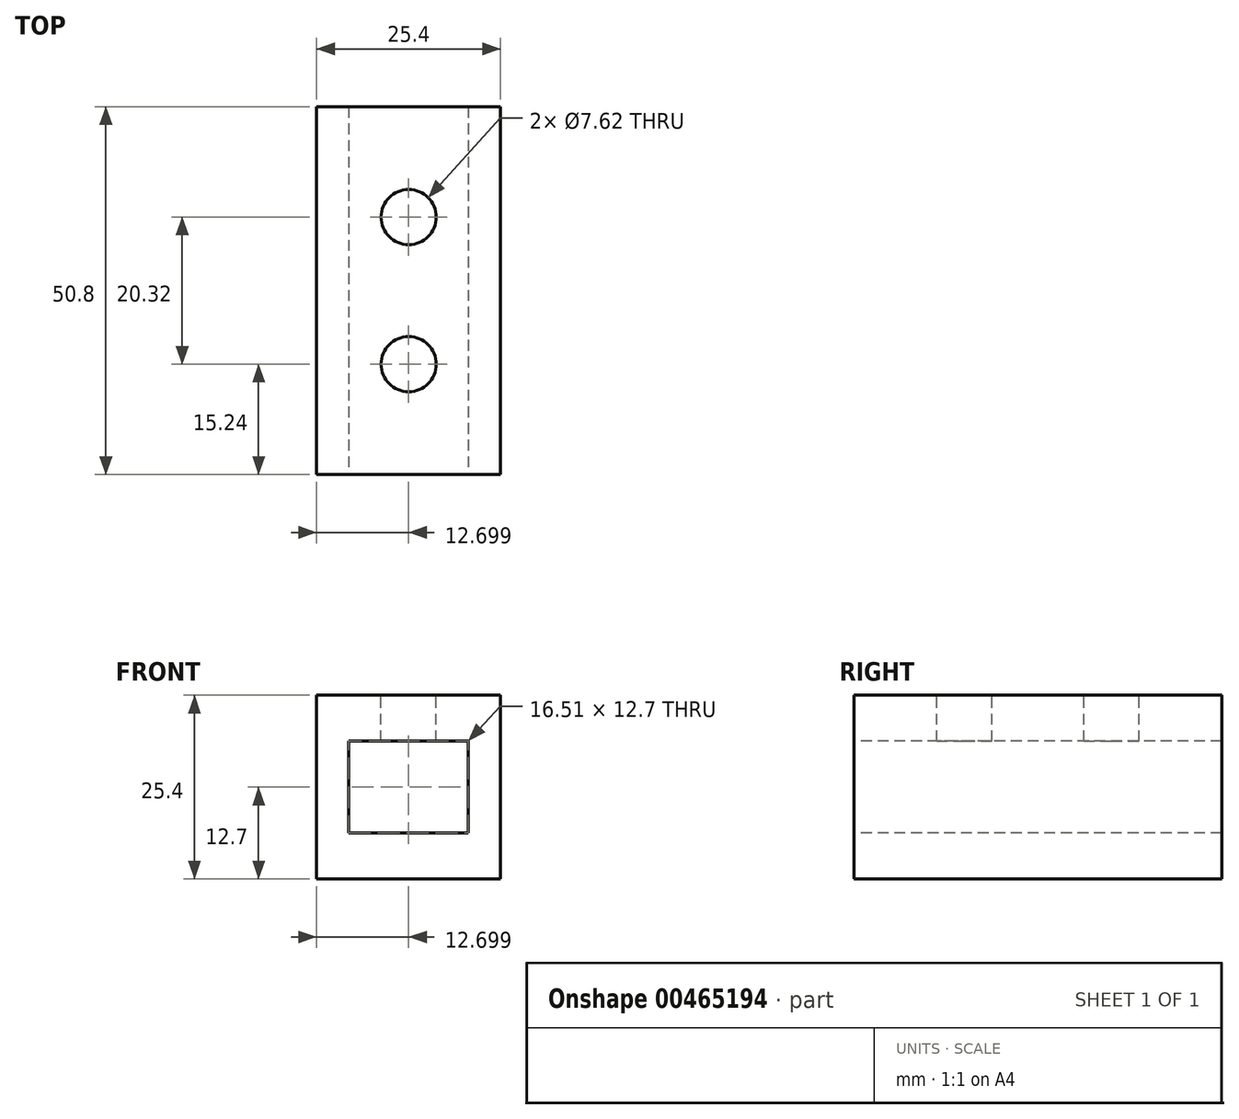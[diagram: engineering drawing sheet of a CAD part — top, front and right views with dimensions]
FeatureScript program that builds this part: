
annotation { "Feature Type Name" : "Feature", "Feature Type Description" : "" }
export const myFeature = defineFeature(function(context is Context, id is Id, definition is map)
    precondition{}
    {
        {
            var Q0;
            Q0=qCreatedBy(makeId("Top.planeOp"),FACE);
            var sketch = newSketch(context, id + "F0", { "sketchPlane" : qUnion([Q0])});
            skLineSegment(sketch, "E0.bottom", {"start": v(14.94, 25.4) * mm, "end": v(-10.46, 25.4) * mm});
            skLineSegment(sketch, "E0.top", {"start": v(14.94, -25.4) * mm, "end": v(-10.46, -25.4) * mm});
            skLineSegment(sketch, "E0.left", {"start": v(14.94, 25.4) * mm, "end": v(14.94, -25.4) * mm});
            skLineSegment(sketch, "E0.right", {"start": v(-10.46, 25.4) * mm, "end": v(-10.46, -25.4) * mm});
            skPoint(sketch, "E0.middle", {"position": v(2.24, 0) * mm});
            skSolve(sketch);
        }
        {
            var Q0;
            Q0=makeQuery(id+"F0.imprint","IMPRINT",FACE,{"disambiguationData":[TD([[makeQuery(id+"F0.imprint","IMPRINT",EDGE,{"derivedFrom":sQuery(id+"F0.wireOp",EDGE,"E0.bottom")}),1.0]])]});
            extrude(context, id + "F1", {"entities" : qUnion([Q0]), "depth" : 25.4 * mm});
        }
        {
            var Q0;
            Q0=makeQuery(id+"F1.opExtrude","SWEPT_FACE",FACE,{"disambiguationData":[OSD([sQuery(id+"F0.wireOp",EDGE,"E0.top")])]});
            var sketch = newSketch(context, id + "F2", { "sketchPlane" : qUnion([Q0])});
            skLineSegment(sketch, "E1.bottom", {"start": v(10.5, 19.05) * mm, "end": v(-6.02, 19.05) * mm});
            skLineSegment(sketch, "E1.top", {"start": v(10.5, 6.35) * mm, "end": v(-6.02, 6.35) * mm});
            skLineSegment(sketch, "E1.left", {"start": v(10.5, 19.05) * mm, "end": v(10.5, 6.35) * mm});
            skLineSegment(sketch, "E1.right", {"start": v(-6.02, 19.05) * mm, "end": v(-6.02, 6.35) * mm});
            skPoint(sketch, "E1.middle", {"position": v(2.24, 12.7) * mm});
            skPoint(sketch, "E1.middle.positionSnap0", {"position": v(-10.46, 12.7) * mm});
            skPoint(sketch, "E1.middle.positionSnap1", {"position": v(2.24, 0) * mm});
            skPoint(sketch, "E1.centerSnap0", {"position": v(-10.46, 12.7) * mm});
            skPoint(sketch, "E1.centerSnap1", {"position": v(2.24, 0) * mm});
            skSolve(sketch);
        }
        {
            var Q0;
            Q0=makeQuery(id+"F2.imprint","IMPRINT",FACE,{"disambiguationData":[TD([[makeQuery(id+"F2.imprint","IMPRINT",EDGE,{"derivedFrom":sQuery(id+"F2.wireOp",EDGE,"E1.bottom")}),1.0]])]});
            extrude(context, id + "F3", {"entities" : qUnion([Q0]), "operationType" : NewBodyOperationType.REMOVE, "oppositeDirection" : true, "depth" : 50.8 * mm});
        }
        {
            var Q0;
            Q0=makeQuery(id+"F1.opExtrude","CAP_FACE",FACE,{"disambiguationData":[OSD([sQuery(id+"F0.wireOp",EDGE,"E0.bottom"),sQuery(id+"F0.wireOp",EDGE,"E0.top"),sQuery(id+"F0.wireOp",EDGE,"E0.left"),sQuery(id+"F0.wireOp",EDGE,"E0.right")])],"isStart":false});
            var sketch = newSketch(context, id + "F4", { "sketchPlane" : qUnion([Q0])});
            skCircle(sketch, "E2", {"center": v(2.24, 10.16) * mm, "radius": 3.81 * mm});
            skPoint(sketch, "E2.centerSnap0", {"position": v(2.24, 25.4) * mm});
            skCircle(sketch, "E3", {"center": v(2.24, -10.16) * mm, "radius": 3.81 * mm});
            skPoint(sketch, "E3.centerSnap0", {"position": v(2.24, -25.4) * mm});
            skSolve(sketch);
        }
        {
            var Q0;
            Q0=makeQuery(id+"F4.imprint","IMPRINT",FACE,{"disambiguationData":[TD([[makeQuery(id+"F4.imprint","IMPRINT",EDGE,{"derivedFrom":sQuery(id+"F4.wireOp",EDGE,"E2")}),1.0]])]});
            var Q1;
            Q1=makeQuery(id+"F4.imprint","IMPRINT",FACE,{"disambiguationData":[TD([[makeQuery(id+"F4.imprint","IMPRINT",EDGE,{"derivedFrom":sQuery(id+"F4.wireOp",EDGE,"E3")}),1.0]])]});
            extrude(context, id + "F5", {"entities" : qUnion([Q0, Q1]), "operationType" : NewBodyOperationType.REMOVE, "oppositeDirection" : true, "depth" : 15.24 * mm});
        }
    });
